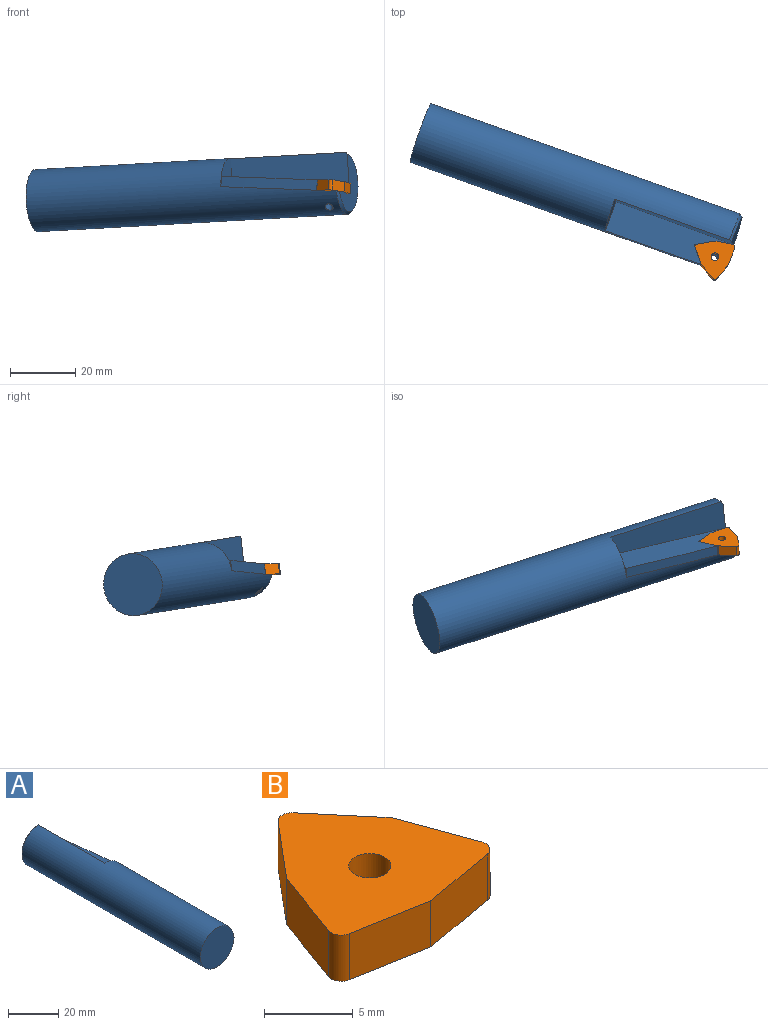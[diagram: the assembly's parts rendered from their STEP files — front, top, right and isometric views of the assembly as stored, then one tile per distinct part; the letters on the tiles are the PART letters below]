
ASSEMBLY  parts=2 mates=1
PART A: 15 faces, bbox 19.1x101.6x19.1 mm
  f0: plane 11.25x9.16mm, normal (0,0.09,1), area 70.3mm2, adj f1,f2,f3,f6,f7,f8,f11,f13
  f1: plane 38.1x12.86mm, normal (1,0,0), area 305.8mm2, adj f0,f2,f3,f5,f9,f12,f13,f14
  f2: cylinder r=9.53mm len=100.84mm, axis (0,1,0), area 5409.1mm2, adj f0,f1,f4,f5,f6,f10,f14
  f3: plane 17.53x16.87mm, normal (0,1,0), area 152.4mm2, adj f0,f1,f14
  f4: plane 19.05x19.05mm, normal (0,-1,0), area 285mm2, adj f2
  f5: plane 9.53x9.53mm, normal (0,1,0), area 71.3mm2, adj f1,f2,f9
  f6: cylinder r=1.19mm len=5.74mm, axis (0,0.09,1), area 35.6mm2, adj f0,f2
  f7: plane 5.9x3.65mm, normal (0.87,0.5,-0.04), area 20.7mm2, adj f0,f8,f11,f12
  f8: plane 5.39x3.61mm, normal (0.98,0.17,-0.02), area 16.5mm2, adj f0,f7,f12,f13
  f9: plane 9.53x3.16mm, normal (0,-1,0.09), area 30.2mm2, adj f1,f5,f10,f12
  f10: extruded ~31.3x5.88mm, area 98.9mm2, adj f2,f9,f11,f12
  f11: plane 4.96x4.42mm, normal (-0.64,0.76,-0.07), area 20.5mm2, adj f0,f7,f10,f12
  f12: plane 37.75x9.53mm, normal (0,0.09,1), area 281.7mm2, adj f1,f7,f8,f9,f10,f11,f13
  f13: plane 3.17x0.41mm, normal (1,0.09,-0.01), area 0.4mm2, adj f0,f1,f8,f12
  f14: cone r=9.53mm half-angle=45deg, axis (0,-1,0), area 42.8mm2, adj f0,f1,f2,f3
PART B: 12 faces, bbox 12.3x11.8x3.2 mm
  f0: plane 4.27x3.58mm, normal (0.77,0.64,0), area 17.7mm2, adj f5,f7,f8,f9
  f1: plane 4.27x3.58mm, normal (-0.77,0.64,0), area 17.7mm2, adj f2,f7,f8,f9
  f2: plane 5.23x3.18mm, normal (-0.94,0.34,0), area 17.7mm2, adj f1,f7,f8,f11
  f3: plane 5.49x3.18mm, normal (-0.17,-0.98,0), area 17.7mm2, adj f4,f7,f8,f11
  f4: plane 5.49x3.18mm, normal (0.17,-0.98,0), area 17.7mm2, adj f3,f7,f8,f10
  f5: plane 5.23x3.18mm, normal (0.94,0.34,0), area 17.7mm2, adj f0,f7,f8,f10
  f6: cylinder r=1.19mm len=3.18mm, axis (0,0,-1), area 23.7mm2, adj f7,f8
  f7: plane 12.28x11.8mm, normal (0,0,1), area 88.1mm2, adj f0,f1,f2,f3,f4,f5,f6,f9
  f8: plane 12.28x11.8mm, normal (0,0,-1), area 88.1mm2, adj f0,f1,f2,f3,f4,f5,f6,f9
  f9: cylinder r=0.79mm len=3.18mm, axis (0,0,1), area 4.4mm2, adj f0,f1,f7,f8
  f10: cylinder r=0.79mm len=3.18mm, axis (0,0,1), area 4.4mm2, adj f4,f5,f7,f8
  f11: cylinder r=0.79mm len=3.18mm, axis (0,0,1), area 4.4mm2, adj f2,f3,f7,f8
PLACE A rot(axis=(-0.03,-0.06,-1),109.9deg) t=(13.65,-2.42,-0.84)mm
PLACE B rot(axis=(-0.1,0.02,-0.99),60.3deg) t=(8.13,-6.53,-3.5)mm
MATE revolute B.f6 <-> A.f6  axis (-0.06,-0.08,-0.99) through (8.13,-6.53,-3.5)mm
